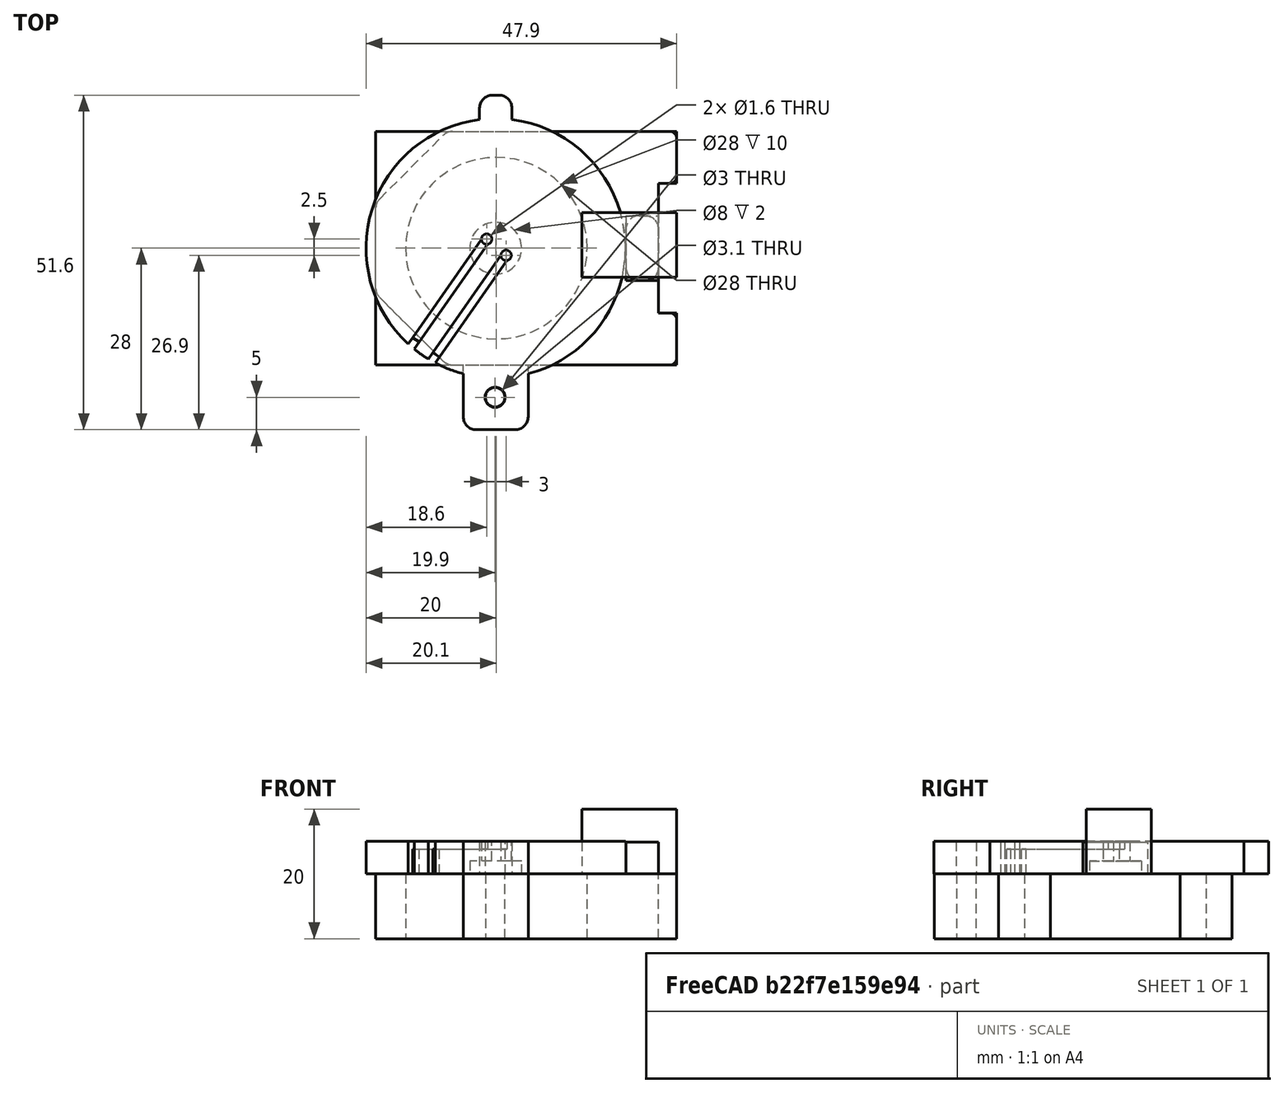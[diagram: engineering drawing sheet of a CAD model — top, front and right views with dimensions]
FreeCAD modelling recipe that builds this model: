
FCSTD DOCUMENT  (FreeCAD 1.0R39319 (Git))
Label: CdSHolderBooleaned3
License: All rights reserved
LicenseURL: https://en.wikipedia.org/wiki/All_rights_reserved
objects: Part::Box×11, Part::Cut×11, Part::Cylinder×7, Part::Fillet×6, Part::Fuse×5, Part::Chamfer×1
note: 41 computed .brp shape members not serialized (recipe doc carries the construction recipe); baked Part::Feature solids carry a one-line shape summary decoded from their .brp

FEATURE [Part::Cylinder] Cylinder  label="cardboardBarrelHolder"
  Angle = 360
  AttacherType = Attacher::AttachEngine3D
  FirstAngle = 0
  Height = 40
  Placement = pos=(-1.1,0,-20) rot=(0,0,1;0rad)
  Radius = 14
  SecondAngle = 0
FEATURE [Part::Box] Box  label="mainPiece"
  AttacherType = Attacher::AttachEngine3D
  Height = 46.4
  Length = 10
  Placement = pos=(-19.7,-18,-4.4e-15) rot=(0,1,0;1.5708rad)
  Width = 36
FEATURE [Part::Box] Box001  label="Cube001"
  AttacherType = Attacher::AttachEngine3D
  Height = 14.6
  Length = 10
  Placement = pos=(12.1,-4.5,10) rot=(0,1,0;1.5708rad)
  Width = 10
FEATURE [Part::Box] Box002  label="hingePinTab"
  AttacherType = Attacher::AttachEngine3D
  Height = 10
  Length = 10
  Placement = pos=(-6.2,-27.952,-10) rot=(0,0,1;0rad)
  Width = 10
FEATURE [Part::Cylinder] Cylinder001  label="hingeTabHole"
  Angle = 360
  AttacherType = Attacher::AttachEngine3D
  FirstAngle = 0
  Height = 30
  Placement = pos=(-1.3,-23,-12) rot=(0,0,1;0rad)
  Radius = 1.5
  SecondAngle = 0
FEATURE [Part::Cylinder] Cylinder002  label="shutter"
  Angle = 360
  AttacherType = Attacher::AttachEngine3D
  FirstAngle = 0
  Height = 5
  Placement = pos=(-1.2,0,0) rot=(0,0,1;0rad)
  Radius = 20
  SecondAngle = 0
FEATURE [Part::Box] Box003  label="shutterHingeTab"
  AttacherType = Attacher::AttachEngine3D
  Height = 5
  Length = 10
  Placement = pos=(-6.2,-28,0) rot=(0,0,1;0rad)
  Width = 14
FEATURE [Part::Box] Box004  label="swivelStop"
  AttacherType = Attacher::AttachEngine3D
  Height = 5
  Length = 5
  Placement = pos=(18.9,-5,-0.1) rot=(0,0,1;0rad)
  Width = 10
FEATURE [Part::Box] Box005  label="footCutout"
  AttacherType = Attacher::AttachEngine3D
  Height = 20
  Length = 10
  Placement = pos=(23.9,-10,-18) rot=(0,0,1;0rad)
  Width = 20
FEATURE [Part::Cylinder] Cylinder003  label="shutterTabHole"
  Angle = 360
  AttacherType = Attacher::AttachEngine3D
  FirstAngle = 0
  Height = 50
  Placement = pos=(-1.3,-23,-12) rot=(0,0,1;0rad)
  Radius = 1.55
  SecondAngle = 0
FEATURE [Part::Box] Box006  label="shutterMoveTab"
  AttacherType = Attacher::AttachEngine3D
  Height = 5
  Length = 5
  Placement = pos=(-3.7,18.6,0) rot=(0,0,1;0rad)
  Width = 5
FEATURE [Part::Cylinder] Cylinder004  label="CdSDivot"
  Angle = 360
  AttacherType = Attacher::AttachEngine3D
  FirstAngle = 0
  Height = 10
  Placement = pos=(-1.2,0,-8) rot=(0,0,1;0rad)
  Radius = 4
  SecondAngle = 0
FEATURE [Part::Cylinder] Cylinder005  label="CdSWire1"
  Angle = 360
  AttacherType = Attacher::AttachEngine3D
  FirstAngle = 0
  Height = 30
  Placement = pos=(0.4,-1.1,-18) rot=(0,0,1;0rad)
  Radius = 0.8
  SecondAngle = 0
FEATURE [Part::Cylinder] Cylinder006  label="CdsWire2"
  Angle = 360
  AttacherType = Attacher::AttachEngine3D
  FirstAngle = 0
  Height = 30
  Placement = pos=(-2.6,1.4,-18) rot=(0,0,1;0rad)
  Radius = 0.8
  SecondAngle = 0
FEATURE [Part::Box] Box007  label="radialTransit1"
  AttacherType = Attacher::AttachEngine3D
  Height = 10
  Length = 1.2
  Placement = pos=(-17.353,-25.3595,3.8) rot=(0,0,1;5.67232rad)
  Width = 30
FEATURE [Part::Box] Box008  label="radialTransit2"
  AttacherType = Attacher::AttachEngine3D
  Height = 10
  Length = 1.2
  Placement = pos=(-20.3756,-22.8768,3.8) rot=(0,0,1;5.67232rad)
  Width = 30
FEATURE [Part::Box] Box009  label="radialTransit3"
  AttacherType = Attacher::AttachEngine3D
  Height = 10
  Length = 1.2
  Placement = pos=(-10.8716,-16.103,-4.1) rot=(-0.913318,0.287968,0.287968;4.62184rad)
  Width = 30
FEATURE [Part::Box] Box010  label="radialTransit4"
  AttacherType = Attacher::AttachEngine3D
  Height = 10
  Length = 1.2
  Placement = pos=(-14.0089,-13.7842,-4.1) rot=(-0.913318,0.287968,0.287968;4.62184rad)
  Width = 30
FEATURE [Part::Cut] Cut
  Base = -> Box
  Tool = -> Cylinder
FEATURE [Part::Cut] Cut001  label="mainPiece1"
  Base = -> Cut
  Tool = -> Box005
FEATURE [Part::Cut] Cut002
  Base = -> Cylinder002
  Tool = -> Cylinder004
FEATURE [Part::Cut] Cut003
  Base = -> Cut002
  Tool = -> Cylinder005
FEATURE [Part::Cut] Cut004
  Base = -> Cut003
  Tool = -> Cylinder006
FEATURE [Part::Cut] Cut005
  Base = -> Cut004
  Tool = -> Box007
FEATURE [Part::Cut] Cut006
  Base = -> Cut005
  Tool = -> Box008
FEATURE [Part::Cut] Cut007
  Base = -> Cut006
  Tool = -> Box009
FEATURE [Part::Cut] Cut008  label="shutter1"
  Base = -> Cut007
  Tool = -> Box010
FEATURE [Part::Cut] Cut009  label="shutterHingeTab001"
  Base = -> Box003
  Tool = -> Cylinder003
FEATURE [Part::Cut] Cut010  label="mainPieceHingeTab"
  Base = -> Box002
  Tool = -> Cylinder001
FEATURE [Part::Fuse] Fusion  label="mainPiece2"
  Base = -> Cut001
  Tool = -> Cut010
FEATURE [Part::Fuse] Fusion001  label="shutter2"
  Base = -> Cut008
  Tool = -> Cut009
FEATURE [Part::Fuse] Fusion002  label="Don'tUsemainPiece3"
  Base = -> Cut001
  Tool = -> Box004
FEATURE [Part::Fuse] Fusion003  label="shutter4"
  Base = -> Fusion001
  Tool = -> Box006
FEATURE [Part::Fuse] Fusion004  label="mainPiece10"
  Base = -> Fusion
  Tool = -> Box004
FEATURE [Part::Fillet] Fillet  label="shutter11"
  Base = -> Fusion003
  EdgeLinks = -> Fusion003 [Edge55,Edge56,Edge89,Edge94]
  Edges = 4 edges r=2: [Edge55,Edge56,Edge89,Edge94]
FEATURE [Part::Fillet] Fillet001
  Base = -> Fusion004
  EdgeLinks = -> Fusion004 [Edge58,Edge63]
  Edges = 2 edges r=2: [Edge58,Edge63]
FEATURE [Part::Fillet] Fillet002
  Base = -> Fillet001
  EdgeLinks = -> Fillet001 [Edge54,Edge62]
  Edges = 2 edges r=1: [Edge54,Edge62]
FEATURE [Part::Fillet] Fillet003
  Base = -> Fillet002
  EdgeLinks = -> Fillet002 [Edge18,Edge32]
  Edges = 2 edges r=1: [Edge18,Edge32]
FEATURE [Part::Fillet] Fillet004
  Base = -> Fillet003
  EdgeLinks = -> Fillet003 [Edge70,Edge72,Edge74,Edge75]
  Edges = 4 edges r=2: [Edge70,Edge72,Edge74,Edge75]
FEATURE [Part::Chamfer] Chamfer
  Base = -> Fillet004
  EdgeLinks = -> Fillet004 [Edge74,Edge76]
  Edges = 2 edges r=11: [Edge74,Edge76]
FEATURE [Part::Fillet] Fillet005  label="mainPieceBooleaned10"
  Base = -> Chamfer
  EdgeLinks = -> Chamfer [Edge29,Edge31,Edge34,Edge36]
  Edges = 4 edges r=2: [Edge29,Edge31,Edge34,Edge36]
